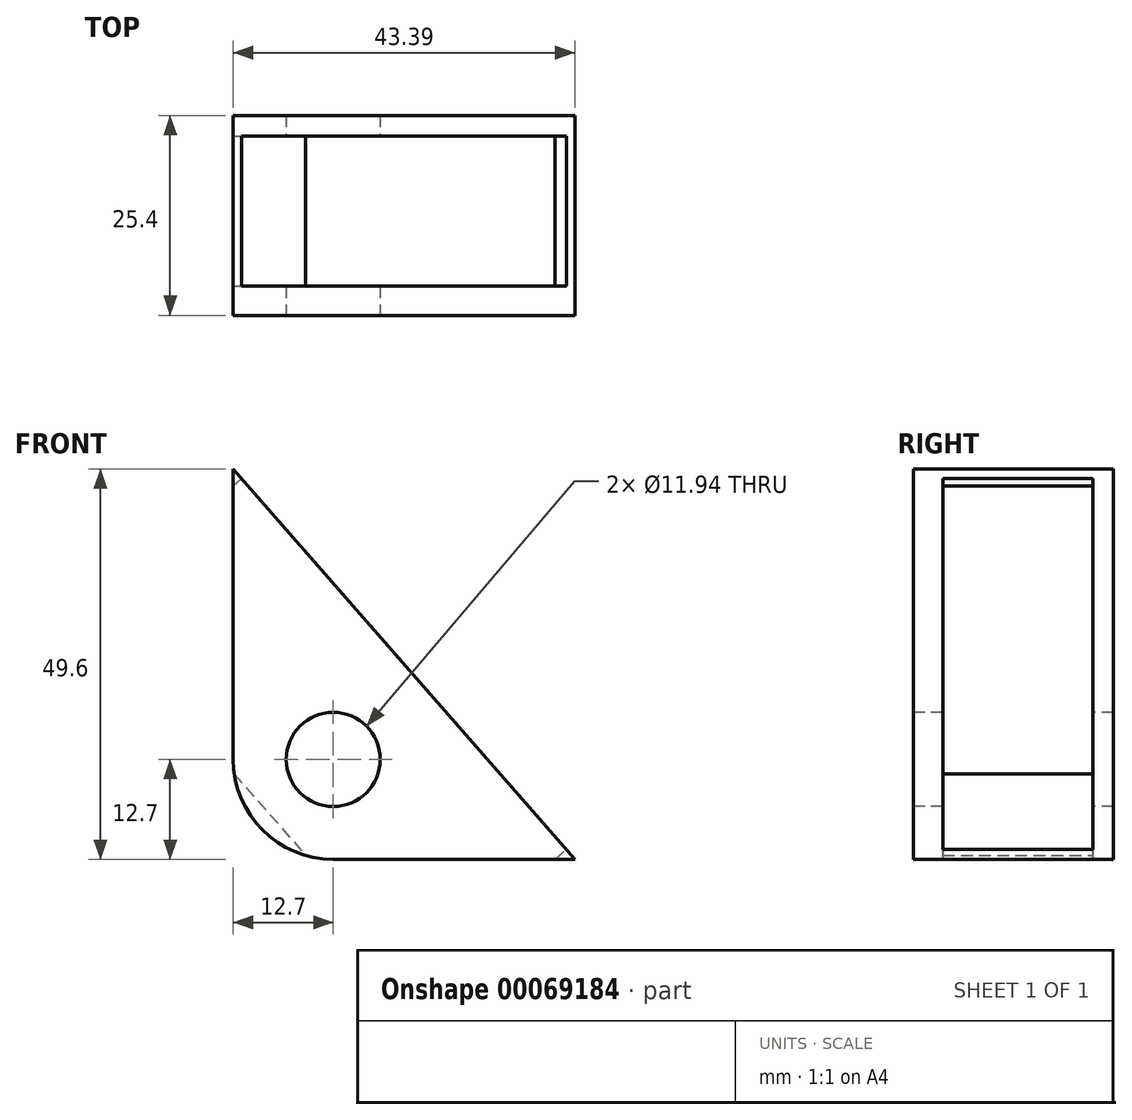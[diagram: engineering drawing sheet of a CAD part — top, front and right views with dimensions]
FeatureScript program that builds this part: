
annotation { "Feature Type Name" : "Feature", "Feature Type Description" : "" }
export const myFeature = defineFeature(function(context is Context, id is Id, definition is map)
    precondition{}
    {
        {
            var Q0;
            Q0=qCreatedBy(makeId("Front.planeOp"),FACE);
            var sketch = newSketch(context, id + "F0", { "sketchPlane" : qUnion([Q0])});
            skLineSegment(sketch, "E0", {"start": v(43.39, 0) * mm, "end": v(0, 0) * mm});
            skLineSegment(sketch, "E1", {"start": v(0, 0) * mm, "end": v(0, 49.6) * mm});
            skLineSegment(sketch, "E2", {"start": v(0, 49.6) * mm, "end": v(43.39, 0) * mm});
            skSolve(sketch);
        }
        {
            var Q0;
            Q0=makeQuery(id+"F0.imprint","IMPRINT",FACE,{"disambiguationData":[TD([[makeQuery(id+"F0.imprint","IMPRINT",EDGE,{"derivedFrom":sQuery(id+"F0.wireOp",EDGE,"E0")}),-1.0]])]});
            extrude(context, id + "F1", {"entities" : qUnion([Q0]), "depth" : 25.4 * mm});
        }
        {
            var Q0;
            Q0=makeQuery(id+"F1.opExtrude","SWEPT_EDGE",EDGE,{"disambiguationData":[OSD([sQuery(id+"F0.wireOp",EDGE,"E0"),sQuery(id+"F0.wireOp",EDGE,"E1")])]});
            fillet(context, id + "F2", {"entities" : qUnion([Q0]), "radius" : 12.7 * mm, "tangentPropagation" : true, "allowEdgeOverflow" : false});
        }
        {
            var Q0;
            Q0=makeQuery(id+"F1.opExtrude","CAP_FACE",FACE,{"disambiguationData":[OSD([sQuery(id+"F0.wireOp",EDGE,"E0"),sQuery(id+"F0.wireOp",EDGE,"E1"),sQuery(id+"F0.wireOp",EDGE,"E2")])],"isStart":false});
            var sketch = newSketch(context, id + "F3", { "sketchPlane" : qUnion([Q0])});
            skCircle(sketch, "E3", {"center": v(12.7, 12.7) * mm, "radius": 5.97 * mm});
            skSolve(sketch);
        }
        {
            var Q0;
            Q0=makeQuery(id+"F3.imprint","IMPRINT",FACE,{"disambiguationData":[TD([[makeQuery(id+"F3.imprint","IMPRINT",EDGE,{"derivedFrom":sQuery(id+"F3.wireOp",EDGE,"E3")}),1.0]])]});
            extrude(context, id + "F4", {"entities" : qUnion([Q0]), "operationType" : NewBodyOperationType.REMOVE, "endBound" : BoundingType.THROUGH_ALL, "oppositeDirection" : true, "depth" : 25.4 * mm});
        }
        {
            var Q0;
            Q0=makeQuery(id+"F1.opExtrude","SWEPT_FACE",FACE,{"disambiguationData":[OSD([sQuery(id+"F0.wireOp",EDGE,"E2")])]});
            var sketch = newSketch(context, id + "F5", { "sketchPlane" : qUnion([Q0])});
            skLineSegment(sketch, "E4.bottom", {"start": v(-2.64, 35.69) * mm, "end": v(-21.7, 35.69) * mm});
            skLineSegment(sketch, "E4.top", {"start": v(-2.64, -26.92) * mm, "end": v(-21.7, -26.92) * mm});
            skLineSegment(sketch, "E4.left", {"start": v(-2.64, 35.69) * mm, "end": v(-2.64, -26.92) * mm});
            skLineSegment(sketch, "E4.right", {"start": v(-21.7, 35.69) * mm, "end": v(-21.7, -26.92) * mm});
            skSolve(sketch);
        }
        {
            var Q0;
            Q0=makeQuery(id+"F5.imprint","IMPRINT",FACE,{"disambiguationData":[TD([[makeQuery(id+"F5.imprint","IMPRINT",EDGE,{"derivedFrom":sQuery(id+"F5.wireOp",EDGE,"E4.bottom")}),1.0]])]});
            extrude(context, id + "F6", {"entities" : qUnion([Q0]), "operationType" : NewBodyOperationType.REMOVE, "oppositeDirection" : true, "depth" : 25.4 * mm});
        }
    });
